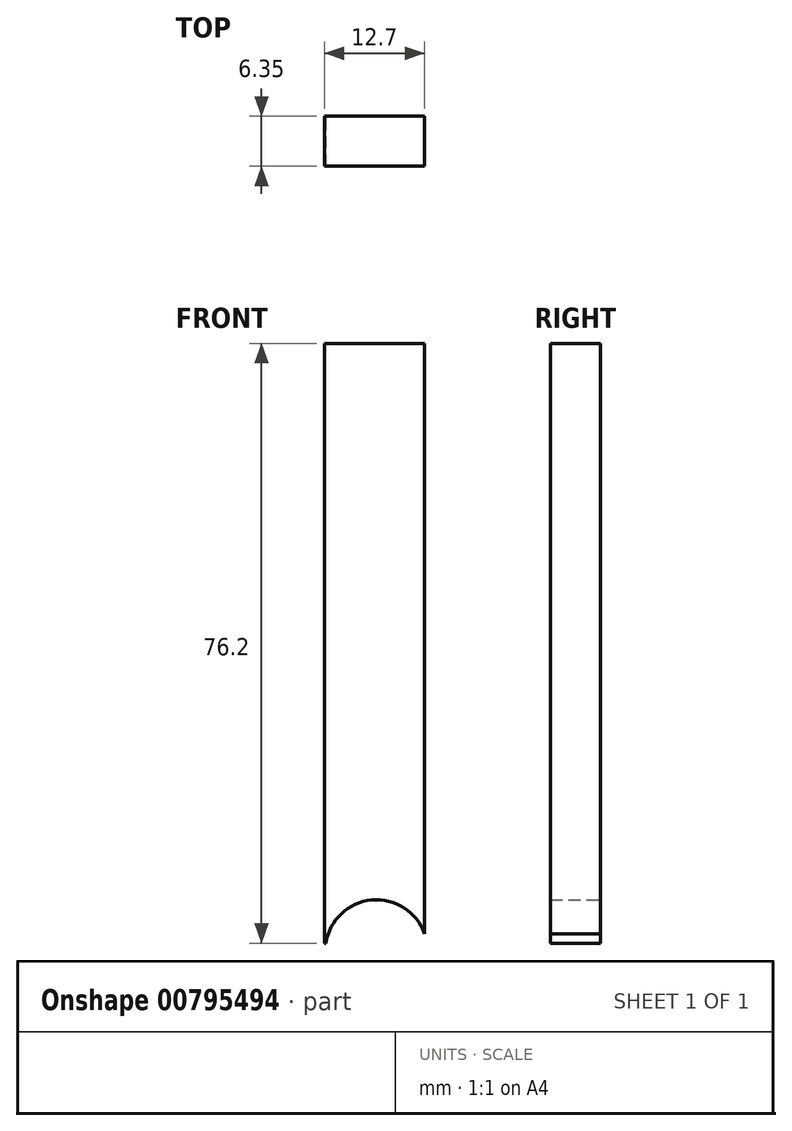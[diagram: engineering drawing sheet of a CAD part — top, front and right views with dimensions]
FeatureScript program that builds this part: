
annotation { "Feature Type Name" : "Feature", "Feature Type Description" : "" }
export const myFeature = defineFeature(function(context is Context, id is Id, definition is map)
    precondition{}
    {
        {
            var Q0;
            Q0=qCreatedBy(makeId("Front.planeOp"),FACE);
            var sketch = newSketch(context, id + "F0", { "sketchPlane" : qUnion([Q0])});
            skLineSegment(sketch, "E0.bottom", {"start": v(-28.2, 43.42) * mm, "end": v(-15.5, 43.42) * mm});
            skLineSegment(sketch, "E0.top", {"start": v(-28.2, -32.78) * mm, "end": v(-15.5, -32.78) * mm});
            skLineSegment(sketch, "E0.left", {"start": v(-28.2, 43.42) * mm, "end": v(-28.2, -32.78) * mm});
            skLineSegment(sketch, "E0.right", {"start": v(-15.5, 43.42) * mm, "end": v(-15.5, -32.78) * mm});
            skSolve(sketch);
        }
        {
            var Q0;
            Q0 = qSketchRegion(id + "F0", true);
            extrude(context, id + "F1", {"entities" : qUnion([Q0]), "depth" : 6.35 * mm, "offsetDistance" : 25.4 * mm});
        }
        {
            var Q0;
            Q0=qCreatedBy(makeId("Front.planeOp"),FACE);
            var sketch = newSketch(context, id + "F2", { "sketchPlane" : qUnion([Q0])});
            skCircle(sketch, "E1", {"center": v(-21.62, -33.73) * mm, "radius": 6.48 * mm});
            skPoint(sketch, "E1.first.point", {"position": v(-28, -32.65) * mm});
            skPoint(sketch, "E1.second.point", {"position": v(-15.24, -32.65) * mm});
            skPoint(sketch, "E1.third.point", {"position": v(-21.33, -40.2) * mm});
            skSolve(sketch);
        }
        {
            var Q0;
            Q0 = qSketchRegion(id + "F2", true);
            extrude(context, id + "F3", {"entities" : qUnion([Q0]), "operationType" : NewBodyOperationType.REMOVE, "endBound" : BoundingType.SYMMETRIC, "depth" : 25.4 * mm, "offsetDistance" : 25.4 * mm});
        }
    });
